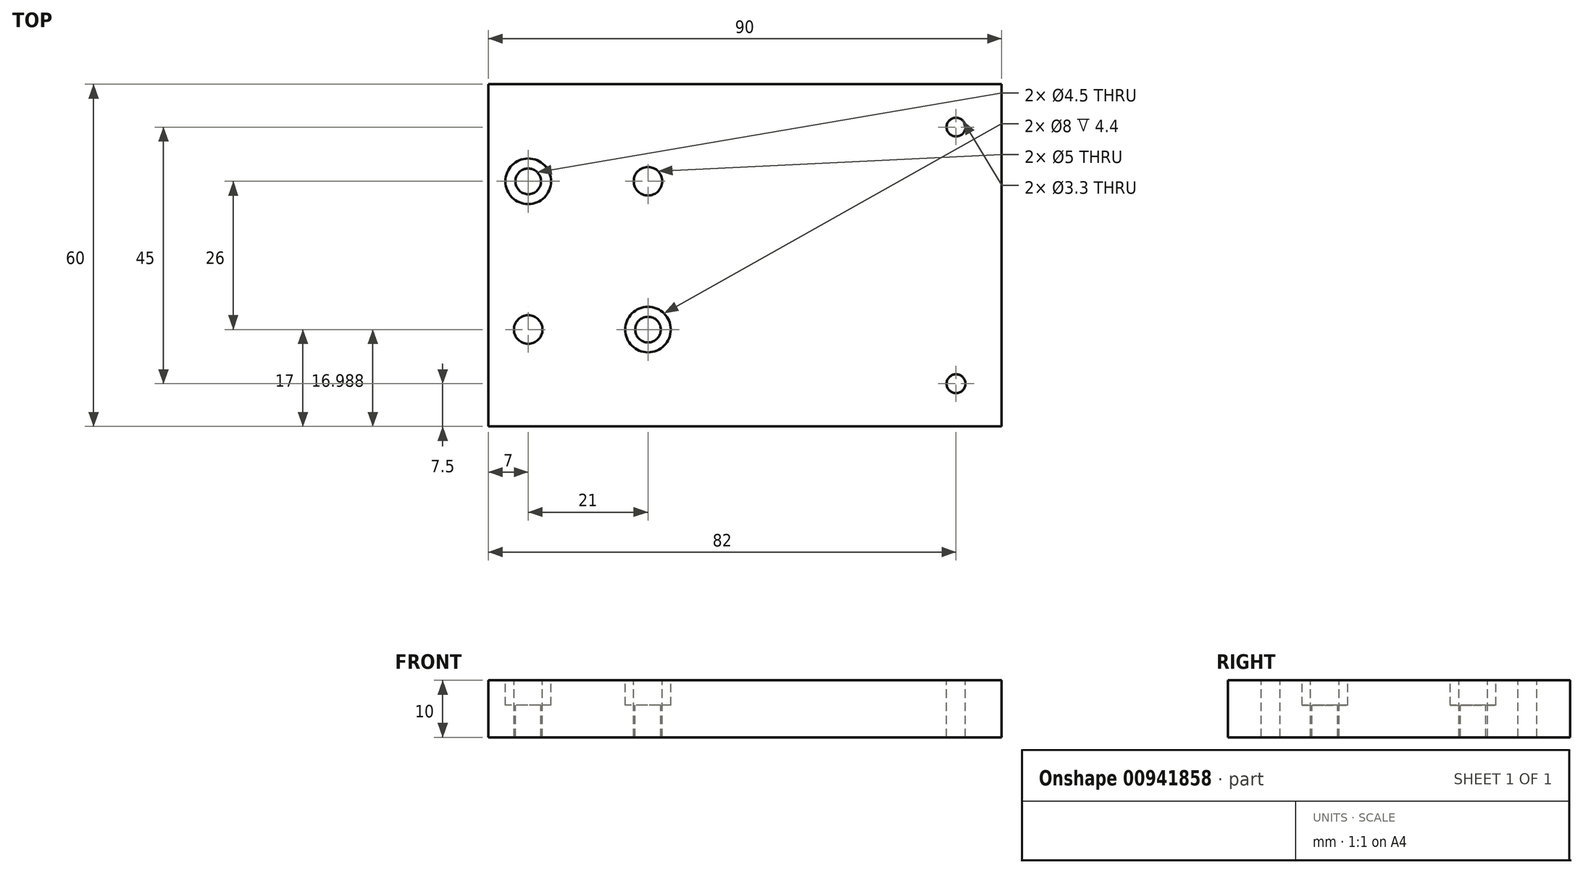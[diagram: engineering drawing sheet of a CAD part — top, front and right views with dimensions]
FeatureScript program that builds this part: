
annotation { "Feature Type Name" : "Feature", "Feature Type Description" : "" }
export const myFeature = defineFeature(function(context is Context, id is Id, definition is map)
    precondition{}
    {
        {
            var Q0;
            Q0=qCreatedBy(makeId("Top.planeOp"),FACE);
            var sketch = newSketch(context, id + "F0", { "sketchPlane" : qUnion([Q0])});
            skLineSegment(sketch, "E0.bottom", {"start": v(45, 30) * mm, "end": v(-45, 30) * mm});
            skLineSegment(sketch, "E0.top", {"start": v(45, -30) * mm, "end": v(-45, -30) * mm});
            skLineSegment(sketch, "E0.left", {"start": v(45, 30) * mm, "end": v(45, -30) * mm});
            skLineSegment(sketch, "E0.right", {"start": v(-45, 30) * mm, "end": v(-45, -30) * mm});
            skPoint(sketch, "E0.middle", {"position": v(0, 0) * mm});
            skSolve(sketch);
        }
        {
            var Q0;
            Q0=makeQuery(id+"F0.imprint","IMPRINT",FACE,{"disambiguationData":[TD([[makeQuery(id+"F0.imprint","IMPRINT",EDGE,{"derivedFrom":sQuery(id+"F0.wireOp",EDGE,"E0.bottom")}),1.0]])]});
            extrude(context, id + "F1", {"entities" : qUnion([Q0]), "depth" : 10 * mm, "offsetDistance" : 25.4 * mm});
        }
        {
            var Q0;
            Q0=makeQuery(id+"F1.opExtrude","CAP_FACE",FACE,{"disambiguationData":[OSD([sQuery(id+"F0.wireOp",EDGE,"E0.bottom"),sQuery(id+"F0.wireOp",EDGE,"E0.top"),sQuery(id+"F0.wireOp",EDGE,"E0.left"),sQuery(id+"F0.wireOp",EDGE,"E0.right")])],"isStart":false});
            var sketch = newSketch(context, id + "F2", { "sketchPlane" : qUnion([Q0])});
            skPoint(sketch, "E1", {"position": v(-38, 12.99) * mm});
            skPoint(sketch, "E2", {"position": v(-17, -13.01) * mm});
            skSolve(sketch);
        }
        {
            var Q0;
            Q0=sQuery(id+"F2.wireOp",VERTEX,"E1");
            var Q1;
            Q1=sQuery(id+"F2.wireOp",VERTEX,"E2");
            var Q2;
            Q2=makeQuery(id+"F1.opExtrude","SWEPT_BODY",BODY,{"disambiguationData":[OSD([sQuery(id+"F0.wireOp",EDGE,"E0.bottom"),sQuery(id+"F0.wireOp",EDGE,"E0.top"),sQuery(id+"F0.wireOp",EDGE,"E0.left"),sQuery(id+"F0.wireOp",EDGE,"E0.right")])]});
            hole(context, id + "F3", {"style" : HoleStyle.C_BORE, "endStyle" : HoleEndStyle.THROUGH, "holeDiameter" : 4.5 * mm, "cBoreDiameter" : 8 * mm, "cBoreDepth" : 4.4 * mm, "majorDiameter" : 5 * mm, "isTappedThrough" : true, "tappedDepth" : 12 * mm, "tapClearance" : 3, "startFromSketch" : true, "locations" : qUnion([Q0, Q1]), "scope" : qUnion([Q2])});
        }
        {
            var Q0;
            Q0=makeQuery(id+"F1.opExtrude","CAP_FACE",FACE,{"disambiguationData":[OSD([sQuery(id+"F0.wireOp",EDGE,"E0.bottom"),sQuery(id+"F0.wireOp",EDGE,"E0.top"),sQuery(id+"F0.wireOp",EDGE,"E0.left"),sQuery(id+"F0.wireOp",EDGE,"E0.right")])],"isStart":false});
            var sketch = newSketch(context, id + "F4", { "sketchPlane" : qUnion([Q0])});
            skPoint(sketch, "E3", {"position": v(-17, 13) * mm});
            skPoint(sketch, "E4", {"position": v(-38, -13) * mm});
            skLineSegment(sketch, "E5", {"start": v(-50.05, 0) * mm, "end": v(49.72, 0) * mm, "construction": true});
            skPoint(sketch, "E5.startSnap0", {"position": v(-45, 0) * mm});
            skSolve(sketch);
        }
        {
            var Q0;
            Q0=sQuery(id+"F4.wireOp",VERTEX,"E4");
            var Q1;
            Q1=sQuery(id+"F4.wireOp",VERTEX,"E3");
            var Q2;
            Q2=makeQuery(id+"F1.opExtrude","SWEPT_BODY",BODY,{"disambiguationData":[OSD([sQuery(id+"F0.wireOp",EDGE,"E0.bottom"),sQuery(id+"F0.wireOp",EDGE,"E0.top"),sQuery(id+"F0.wireOp",EDGE,"E0.left"),sQuery(id+"F0.wireOp",EDGE,"E0.right")])]});
            hole(context, id + "F5", {"style" : HoleStyle.SIMPLE, "endStyle" : HoleEndStyle.THROUGH, "standardTappedOrClearance" : lookupTablePath({ "standard" : "ISO", "size" : "5", "type" : "Drilled" }), "standardBlindInLast" : lookupTablePath({ "standard" : "ISO", "size" : "5", "type" : "Drilled" }), "holeDiameter" : 5 * mm, "majorDiameter" : 5 * mm, "isTappedThrough" : true, "tappedDepth" : 12 * mm, "tapClearance" : 3, "startFromSketch" : true, "locations" : qUnion([Q0, Q1]), "scope" : qUnion([Q2])});
        }
        {
            var Q0;
            Q0=makeQuery(id+"F1.opExtrude","CAP_FACE",FACE,{"disambiguationData":[OSD([sQuery(id+"F0.wireOp",EDGE,"E0.bottom"),sQuery(id+"F0.wireOp",EDGE,"E0.top"),sQuery(id+"F0.wireOp",EDGE,"E0.left"),sQuery(id+"F0.wireOp",EDGE,"E0.right")])],"isStart":false});
            var sketch = newSketch(context, id + "F6", { "sketchPlane" : qUnion([Q0])});
            skPoint(sketch, "E6", {"position": v(37, 22.5) * mm});
            skPoint(sketch, "E7", {"position": v(37, -22.5) * mm});
            skLineSegment(sketch, "E8", {"start": v(0, 0) * mm, "end": v(63.7, 0) * mm, "construction": true});
            skSolve(sketch);
        }
        {
            var Q0;
            Q0=sQuery(id+"F6.wireOp",VERTEX,"E6");
            var Q1;
            Q1=sQuery(id+"F6.wireOp",VERTEX,"E7");
            var Q2;
            Q2=makeQuery(id+"F1.opExtrude","SWEPT_BODY",BODY,{"disambiguationData":[OSD([sQuery(id+"F0.wireOp",EDGE,"E0.bottom"),sQuery(id+"F0.wireOp",EDGE,"E0.top"),sQuery(id+"F0.wireOp",EDGE,"E0.left"),sQuery(id+"F0.wireOp",EDGE,"E0.right")])]});
            hole(context, id + "F7", {"style" : HoleStyle.SIMPLE, "endStyle" : HoleEndStyle.THROUGH, "standardTappedOrClearance" : lookupTablePath({ "standard" : "ISO", "engagement" : "75%", "pitch" : "0.7 mm", "size" : "M4", "type" : "Tapped" }), "standardBlindInLast" : lookupTablePath({ "standard" : "ISO", "fit" : "Normal", "engagement" : "75%", "pitch" : "0.7 mm", "size" : "M4", "type" : "Clearance & tapped" }), "holeDiameter" : 3.3 * mm, "majorDiameter" : 4 * mm, "showTappedDepth" : true, "isTappedThrough" : true, "tappedDepth" : 12 * mm, "tapClearance" : 3, "startFromSketch" : true, "locations" : qUnion([Q0, Q1]), "scope" : qUnion([Q2])});
        }
    });
